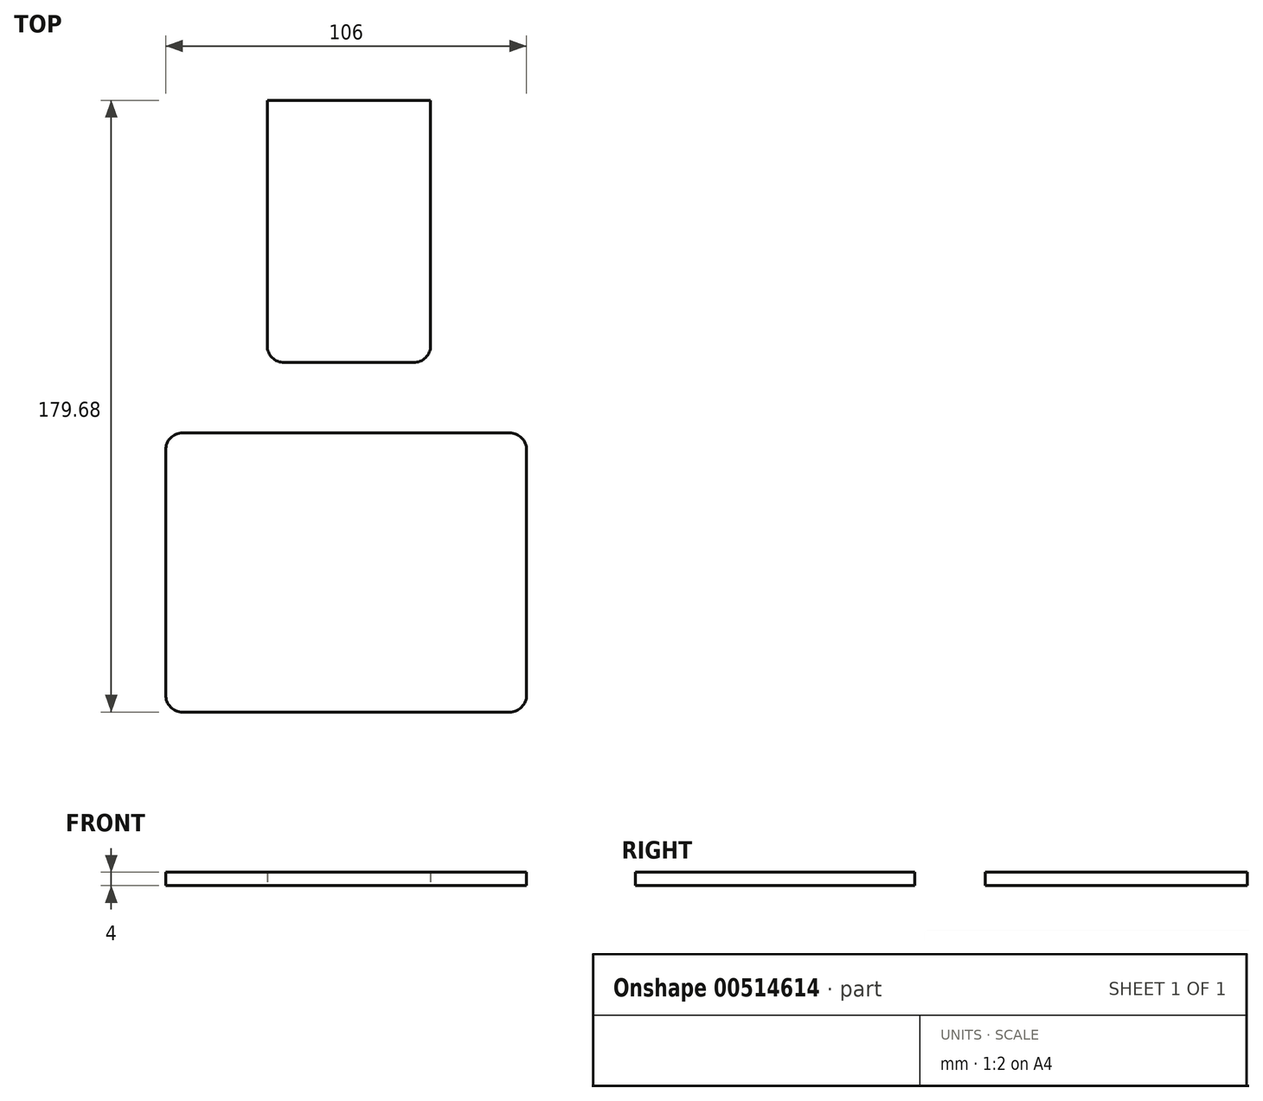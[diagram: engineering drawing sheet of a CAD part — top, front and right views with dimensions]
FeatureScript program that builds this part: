
annotation { "Feature Type Name" : "Feature", "Feature Type Description" : "" }
export const myFeature = defineFeature(function(context is Context, id is Id, definition is map)
    precondition{}
    {
        {
            var Q0;
            Q0=qCreatedBy(makeId("Top.planeOp"),FACE);
            var sketch = newSketch(context, id + "F0", { "sketchPlane" : qUnion([Q0])});
            skLineSegment(sketch, "E0.top", {"start": v(53, -84.5) * mm, "end": v(-53, -84.5) * mm});
            skLineSegment(sketch, "E0.left", {"start": v(53, -2.5) * mm, "end": v(53, -84.5) * mm});
            skLineSegment(sketch, "E0.right", {"start": v(-53, -2.5) * mm, "end": v(-53, -84.5) * mm});
            skPoint(sketch, "E1.orphan", {"position": v(-53, 84.5) * mm});
            skPoint(sketch, "E2.orphan", {"position": v(53, 84.5) * mm});
            skLineSegment(sketch, "E3", {"start": v(-53, -2.5) * mm, "end": v(53, -2.5) * mm});
            skPoint(sketch, "E4.orphan", {"position": v(-53, 7.5) * mm});
            skPoint(sketch, "E5.end.orphan", {"position": v(15.62, 57.1) * mm});
            skPoint(sketch, "E6.orphan", {"position": v(24, 46) * mm});
            skPoint(sketch, "E7.start.orphan", {"position": v(-24, 46) * mm});
            skPoint(sketch, "E8.start.orphan", {"position": v(-18.78, 34.9) * mm});
            skPoint(sketch, "E9.orphan", {"position": v(-45, -2.5) * mm});
            skPoint(sketch, "E10.orphan", {"position": v(45, -2.5) * mm});
            skPoint(sketch, "E11.start.orphan", {"position": v(-18.78, 77.6) * mm});
            skPoint(sketch, "E12.orphan", {"position": v(24, 57.1) * mm});
            skPoint(sketch, "E13", {"position": v(0, 101.9) * mm});
            skPoint(sketch, "E14.end.orphan", {"position": v(50.45, 84.5) * mm});
            skPoint(sketch, "E15.trimOffspring.start.orphan", {"position": v(26.9, 84.5) * mm});
            skPoint(sketch, "E16.end.orphan", {"position": v(0.05, 10.43) * mm});
            skPoint(sketch, "E16.start.orphan", {"position": v(-23.5, 12.91) * mm});
            skPoint(sketch, "E17.orphan", {"position": v(23.5, 57.1) * mm});
            skPoint(sketch, "E18.orphan", {"position": v(24, 7.5) * mm});
            skPoint(sketch, "E19.orphan", {"position": v(-24, 7.5) * mm});
            skPoint(sketch, "E20.end.orphan", {"position": v(-23.5, 32.3) * mm});
            skPoint(sketch, "E20.start.orphan", {"position": v(-23.5, 14.75) * mm});
            skPoint(sketch, "E21.start.orphan", {"position": v(-23.5, 34.8) * mm});
            skPoint(sketch, "E22.right.start.orphan", {"position": v(24, 84.5) * mm});
            skPoint(sketch, "E23.end.orphan", {"position": v(23.5, 59.6) * mm});
            skPoint(sketch, "E23.start.orphan", {"position": v(23.5, 77.5) * mm});
            skPoint(sketch, "E22.bottom.start.orphan", {"position": v(-24, 84.5) * mm});
            skPoint(sketch, "E24.orphan", {"position": v(5, 7.5) * mm});
            skPoint(sketch, "E25.orphan", {"position": v(-5, 7.5) * mm});
            skSolve(sketch);
        }
        {
            var Q0;
            Q0=qCreatedBy(makeId("Top.planeOp"),FACE);
            var sketch = newSketch(context, id + "F1", { "sketchPlane" : qUnion([Q0])});
            skLineSegment(sketch, "E26.bottom", {"start": v(24.82, 95.18) * mm, "end": v(-23.18, 95.18) * mm});
            skLineSegment(sketch, "E27.top", {"start": v(-23.18, 18.18) * mm, "end": v(24.82, 18.18) * mm});
            skLineSegment(sketch, "E27.left", {"start": v(-23.18, 95.18) * mm, "end": v(-23.18, 18.18) * mm});
            skLineSegment(sketch, "E27.right", {"start": v(24.82, 95.18) * mm, "end": v(24.82, 18.18) * mm});
            skPoint(sketch, "E28.orphan", {"position": v(-52.18, 95.18) * mm});
            skPoint(sketch, "E29.orphan", {"position": v(53.82, 95.18) * mm});
            skLineSegment(sketch, "E30.top", {"start": v(5.82, 18.18) * mm, "end": v(-4.18, 18.18) * mm});
            skPoint(sketch, "E31.orphan", {"position": v(-52.18, 18.18) * mm});
            skLineSegment(sketch, "E32", {"start": v(-23.18, 95.18) * mm, "end": v(-23.18, 88.18) * mm});
            skPoint(sketch, "E33.orphan", {"position": v(24.82, 56.68) * mm});
            skPoint(sketch, "E34.start.orphan", {"position": v(-23.18, 56.68) * mm});
            skPoint(sketch, "E35.orphan", {"position": v(-44.18, 8.18) * mm});
            skPoint(sketch, "E36.orphan", {"position": v(45.82, 8.18) * mm});
            skPoint(sketch, "E37.start.orphan", {"position": v(-17.96, 88.28) * mm});
            skPoint(sketch, "E38.orphan", {"position": v(24.82, 67.78) * mm});
            skPoint(sketch, "E39", {"position": v(0.82, 112.58) * mm});
            skPoint(sketch, "E40.end.orphan", {"position": v(51.26, 95.18) * mm});
            skPoint(sketch, "E41.trimOffspring.start.orphan", {"position": v(27.71, 95.18) * mm});
            skPoint(sketch, "E42.end.orphan", {"position": v(0.87, 21.1) * mm});
            skPoint(sketch, "E26.right.end.orphan", {"position": v(-52.18, -73.82) * mm});
            skPoint(sketch, "E26.left.end.orphan", {"position": v(53.82, -73.82) * mm});
            skPoint(sketch, "E43.end.orphan", {"position": v(24.32, 26.57) * mm});
            skSolve(sketch);
        }
        {
            var Q0;
            Q0=makeQuery(id+"F0.imprint","IMPRINT",FACE,{"disambiguationData":[TD([[makeQuery(id+"F0.imprint","IMPRINT",EDGE,{"derivedFrom":sQuery(id+"F0.wireOp",EDGE,"E0.top")}),-1.0]])]});
            var Q1;
            Q1=makeQuery(id+"F1.imprint","IMPRINT",FACE,{"disambiguationData":[TD([[makeQuery(id+"F1.imprint","IMPRINT",EDGE,{"derivedFrom":sQuery(id+"F1.wireOp",EDGE,"E26.bottom")}),1.0]])]});
            var Q2;
            {var subQ5=sQuery(id+"F1.wireOp",EDGE,"56e8594c-ecf8-4cb0-9939-2472721651db");Q2=makeQuery(id+"F1.imprint","IMPRINT",FACE,{"disambiguationData":[TD([[makeQuery(id+"F1.imprint","IMPRINT",EDGE,{"derivedFrom":subQ5}),-1.0]])]});}
            var Q3;
            Q3=makeQuery(id+"F1.imprint","IMPRINT",FACE,{"disambiguationData":[TD([[makeQuery(id+"F1.imprint","IMPRINT",EDGE,{"derivedFrom":sQuery(id+"F1.wireOp",EDGE,"E30.top")}),1.0]])]});
            var Q4;
            Q4=makeQuery(id+"F0.imprint","IMPRINT",FACE,{"disambiguationData":[TD([[makeQuery(id+"F0.imprint","IMPRINT",EDGE,{"derivedFrom":sQuery(id+"F0.wireOp",EDGE,"waGpoIm7-0Mzt-1UnA-IRLj-dOBubJTwNrkn.bottom")}),-1.0]])]});
            var Q5;
            Q5=makeQuery(id+"F1.imprint","IMPRINT",FACE,{"disambiguationData":[TD([[makeQuery(id+"F1.imprint","IMPRINT",EDGE,{"derivedFrom":sQuery(id+"F1.wireOp",EDGE,"5a77a93a-04a2-4624-8db7-a53228818b46")}),1.0]])]});
            var Q6;
            Q6=makeQuery(id+"F1.imprint","IMPRINT",FACE,{"disambiguationData":[TD([[makeQuery(id+"F1.imprint","IMPRINT",EDGE,{"derivedFrom":sQuery(id+"F1.wireOp",EDGE,"64439ff4-f162-4608-b04a-86becdaf6998")}),1.0]])]});
            extrude(context, id + "F2", {"entities" : qUnion([Q0, Q1, Q2, Q3, Q4, Q5, Q6]), "depth" : 4 * mm});
        }
        {
            var Q0;
            Q0=makeQuery(id+"F2.opExtrude","SWEPT_EDGE",EDGE,{"disambiguationData":[OSD([sQuery(id+"F0.wireOp",EDGE,"E0.top"),sQuery(id+"F0.wireOp",EDGE,"E0.left")])]});
            var Q1;
            Q1=makeQuery(id+"F2.opExtrude","SWEPT_EDGE",EDGE,{"disambiguationData":[OSD([sQuery(id+"F0.wireOp",EDGE,"E0.top"),sQuery(id+"F0.wireOp",EDGE,"E0.right")])]});
            var Q2;
            Q2=makeQuery(id+"F2.opExtrude","SWEPT_EDGE",EDGE,{"disambiguationData":[OSD([sQuery(id+"F0.wireOp",EDGE,"E0.right"),sQuery(id+"F0.wireOp",EDGE,"E3")])]});
            var Q3;
            Q3=makeQuery(id+"F2.opExtrude","SWEPT_EDGE",EDGE,{"disambiguationData":[OSD([sQuery(id+"F0.wireOp",EDGE,"E0.left"),sQuery(id+"F0.wireOp",EDGE,"E3")])]});
            var Q4;
            Q4=makeQuery(id+"F2.opExtrude","SWEPT_EDGE",EDGE,{"disambiguationData":[OSD([sQuery(id+"F1.wireOp",EDGE,"E27.top"),sQuery(id+"F1.wireOp",EDGE,"E27.left")])]});
            var Q5;
            Q5=makeQuery(id+"F2.opExtrude","SWEPT_EDGE",EDGE,{"disambiguationData":[OSD([sQuery(id+"F1.wireOp",EDGE,"E27.top"),sQuery(id+"F1.wireOp",EDGE,"E27.right")])]});
            fillet(context, id + "F3", {"entities" : qUnion([Q0, Q1, Q2, Q3, Q4, Q5]), "radius" : 5 * mm, "tangentPropagation" : true, "allowEdgeOverflow" : false});
        }
    });
